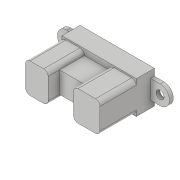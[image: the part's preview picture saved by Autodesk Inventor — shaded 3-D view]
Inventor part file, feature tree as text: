
AUTODESK INVENTOR PART (.ipt)
format: ipt  version: 2018.3 (Build 223284000, 284)  size: 244,736 bytes
history: native  units: in
note: dims shown in document units (in); Inventor stores cm internally (conversion verified against a paired STEP export)
features: extrude x9, sketch x9, fillet x1, plane x1
ambient origin geometry x8: Origin, YZ Plane, XZ Plane, XY Plane, X Axis, Y Axis, Z Axis, Center Point
bodies: Solid1 (feature_tree)
feature tree (20):
  extrude  "Extrusion1"  Depth=0.8504in TaperAngle=0.0deg
  extrude  "Extrusion2"  Depth=0.3976in
  extrude  "Extrusion3"  Depth=0.5669in TaperAngle=0.0deg
  extrude  "Extrusion4"  Depth=0.4114in
  fillet  "Fillet1"  Radius=0.4685in
  extrude  "Extrusion5"  Depth=0.0215in
  extrude  "Extrusion6"  Depth=0.5669in TaperAngle=0.0deg
  extrude  "Extrusion7"  Depth=0.3307in
  plane  "Work Plane5"
  extrude  "Extrusion8"  Depth=0.3898in TaperAngle=0.0deg
  extrude  "Extrusion9"  Depth=0.0472in
  sketch  "Sketch1"  dims[d1=0.7441in d2=0.8504in d3=0.0in]
  sketch  "Sketch2"  dims[d6=0.5118in d11=0.3976in]
  sketch  "Sketch4"  dims[d16=0.8504in d17=0.0in d20=0.5669in d21=0.0in]
  sketch  "Sketch5"  dims[d22=0.3524in d23=0.4114in d24=0.4685in]
  sketch  "Sketch6"  dims[d25=0.4685in d26=0.0215in]
  sketch  "Sketch8"  dims[d27=0.0215in d28=0.5669in d29=0.0in]
  sketch  "Sketch10"  dims[d30=0.0689in d31=0.3307in]
  sketch  "Sketch11"  dims[d32=0.0905in d33=0.3898in d34=0.0in]
  sketch  "Sketch12"  dims[d39=0.3815in d40=1.4567in d41=0.2953in d42=0.126in d43=0.2953in d44=0.126in d46=1.1614in d47=0.0591in d48=0.0in d51=0.2362in d52=0.0in d53=-0.1299in d54=0.0472in d55=0.0in d56=0.0472in d57=0.0in]
